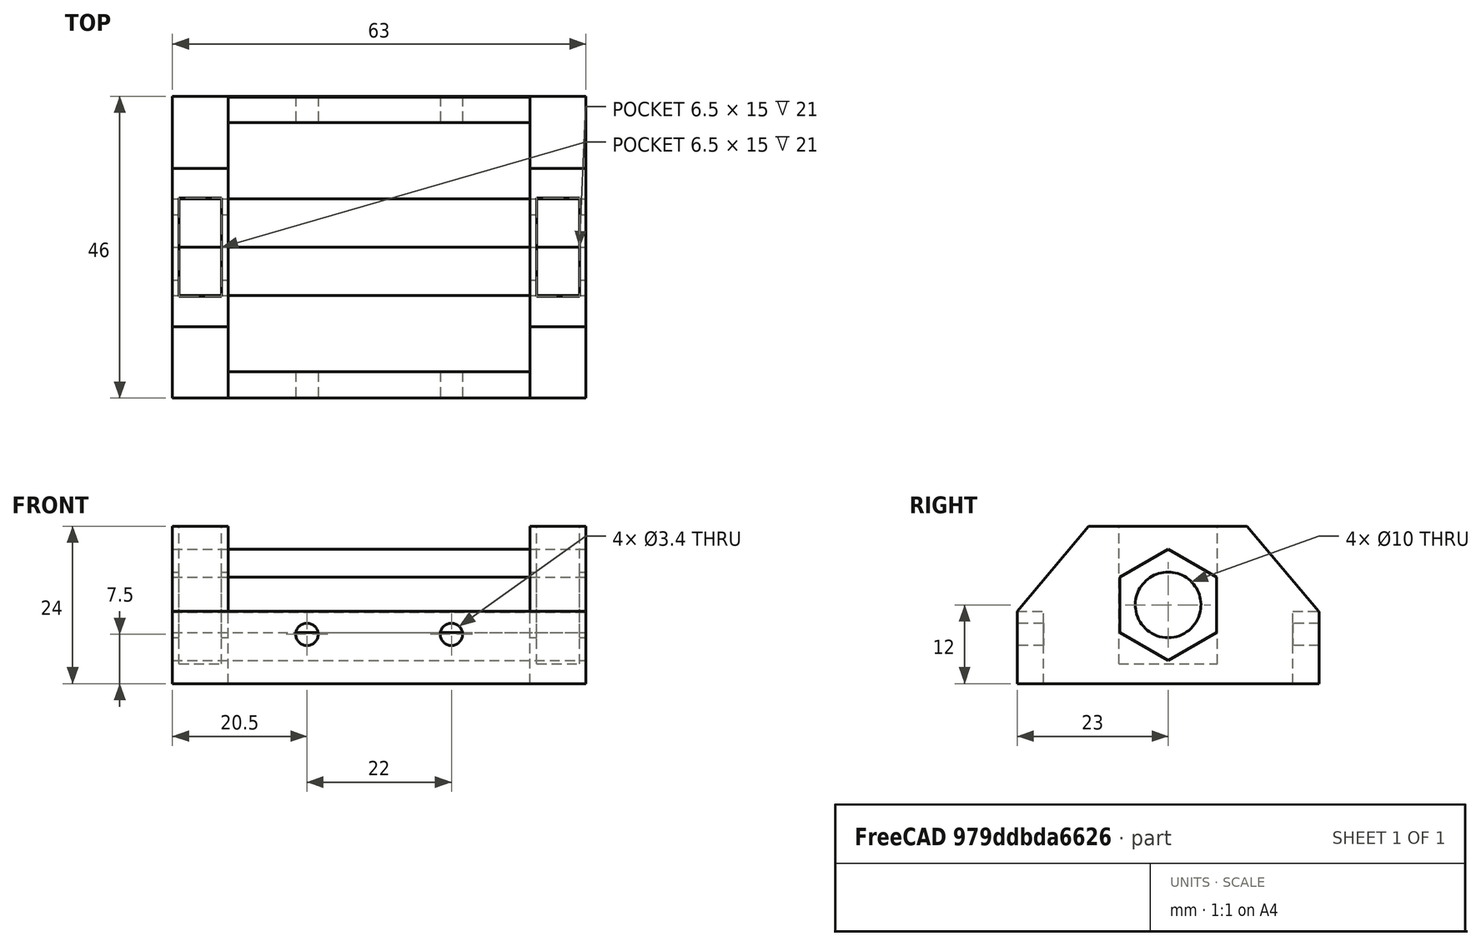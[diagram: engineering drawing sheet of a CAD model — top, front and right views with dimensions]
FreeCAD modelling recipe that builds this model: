
FCSTD DOCUMENT  (FreeCAD 0.14R3702 (Git))
Label: fijacion_eje_x
License: CC-BY 3.0
LicenseURL: http://creativecommons.org/licenses/by/3.0/
objects: Part::Box×8, Part::Cut×8, Part::Cylinder×3, Part::MultiFuse×2, Part::Prism×1
note: 22 computed .brp shape members not serialized (recipe doc carries the construction recipe); baked Part::Feature solids carry a one-line shape summary decoded from their .brp

FEATURE [Part::Box] Box  label="Cubo"
  Height = 11
  Length = 63
  Placement = pos=(0,0,-4) rot=(0,0,1;0rad)
  Width = 46
FEATURE [Part::Box] Box001  label="Cubo001"
  Height = 11
  Length = 46
  Placement = pos=(8.5,4,-4) rot=(0,0,1;0rad)
  Width = 38
FEATURE [Part::Cylinder] Cylinder  label="Cilindro"
  Angle = 360
  Height = 46
  Placement = pos=(20.5,46,3.5) rot=(1,0,0;1.5708rad)
  Radius = 1.7
FEATURE [Part::Cylinder] Cylinder001  label="Cilindro001"
  Angle = 360
  Height = 46
  Placement = pos=(42.5,46,3.5) rot=(1,0,0;1.5708rad)
  Radius = 1.7
FEATURE [Part::Cut] Cut
  Base = -> Box
  Tool = -> Box001
FEATURE [Part::Cut] Cut001
  Base = -> Cut
  Tool = -> Cylinder
FEATURE [Part::Cut] Cut002
  Base = -> Cut001
  Tool = -> Cylinder001
FEATURE [Part::Cylinder] Cylinder002  label="Cilindro002"
  Angle = 360
  Height = 63
  Placement = pos=(0,23,8) rot=(0,1,0;1.5708rad)
  Radius = 5
FEATURE [Part::Box] Box002  label="Cubo002"
  Height = 24
  Length = 8.5
  Placement = pos=(0,0,-4) rot=(0,0,1;0rad)
  Width = 46
FEATURE [Part::Box] Box003  label="Cubo003"
  Height = 24
  Length = 8.5
  Placement = pos=(54.5,0,-4) rot=(0,0,1;0rad)
  Width = 46
FEATURE [Part::Prism] Prism  label="Prisma"
  Circumradius = 8.5
  Height = 63
  Placement = pos=(0,23,8) rot=(0,1,0;1.5708rad)
  Polygon = 6
FEATURE [Part::MultiFuse] Fusion
  Shapes = -> [Cut002,Box002]
FEATURE [Part::MultiFuse] Fusion001
  Shapes = -> [Fusion,Box003]
FEATURE [Part::Cut] Cut003
  Base = -> Fusion001
  Tool = -> Cylinder002
FEATURE [Part::Box] Box004  label="Cubo004"
  Height = 25
  Length = 6.5
  Placement = pos=(1,15.5,-1) rot=(0,0,1;0rad)
  Width = 15
FEATURE [Part::Box] Box005  label="Cubo005"
  Height = 25
  Length = 6.5
  Placement = pos=(55.5,15.5,-1) rot=(0,0,1;0rad)
  Width = 15
FEATURE [Part::Cut] Cut004
  Base = -> Cut003
  Tool = -> Box004
FEATURE [Part::Cut] Cut005
  Base = -> Cut004
  Tool = -> Box005
FEATURE [Part::Box] Box006  label="Cubo006"
  Height = 10
  Length = 63
  Placement = pos=(0,0,7) rot=(1,0,0;0.872665rad)
  Width = 40
FEATURE [Part::Cut] Cut006
  Base = -> Cut005
  Tool = -> Box006
FEATURE [Part::Box] Box007  label="Cubo007"
  Height = 10
  Length = 63
  Placement = pos=(0,35,20) rot=(-1,0,0;0.872665rad)
  Width = 40
FEATURE [Part::Cut] Cut007
  Base = -> Cut006
  Tool = -> Box007
